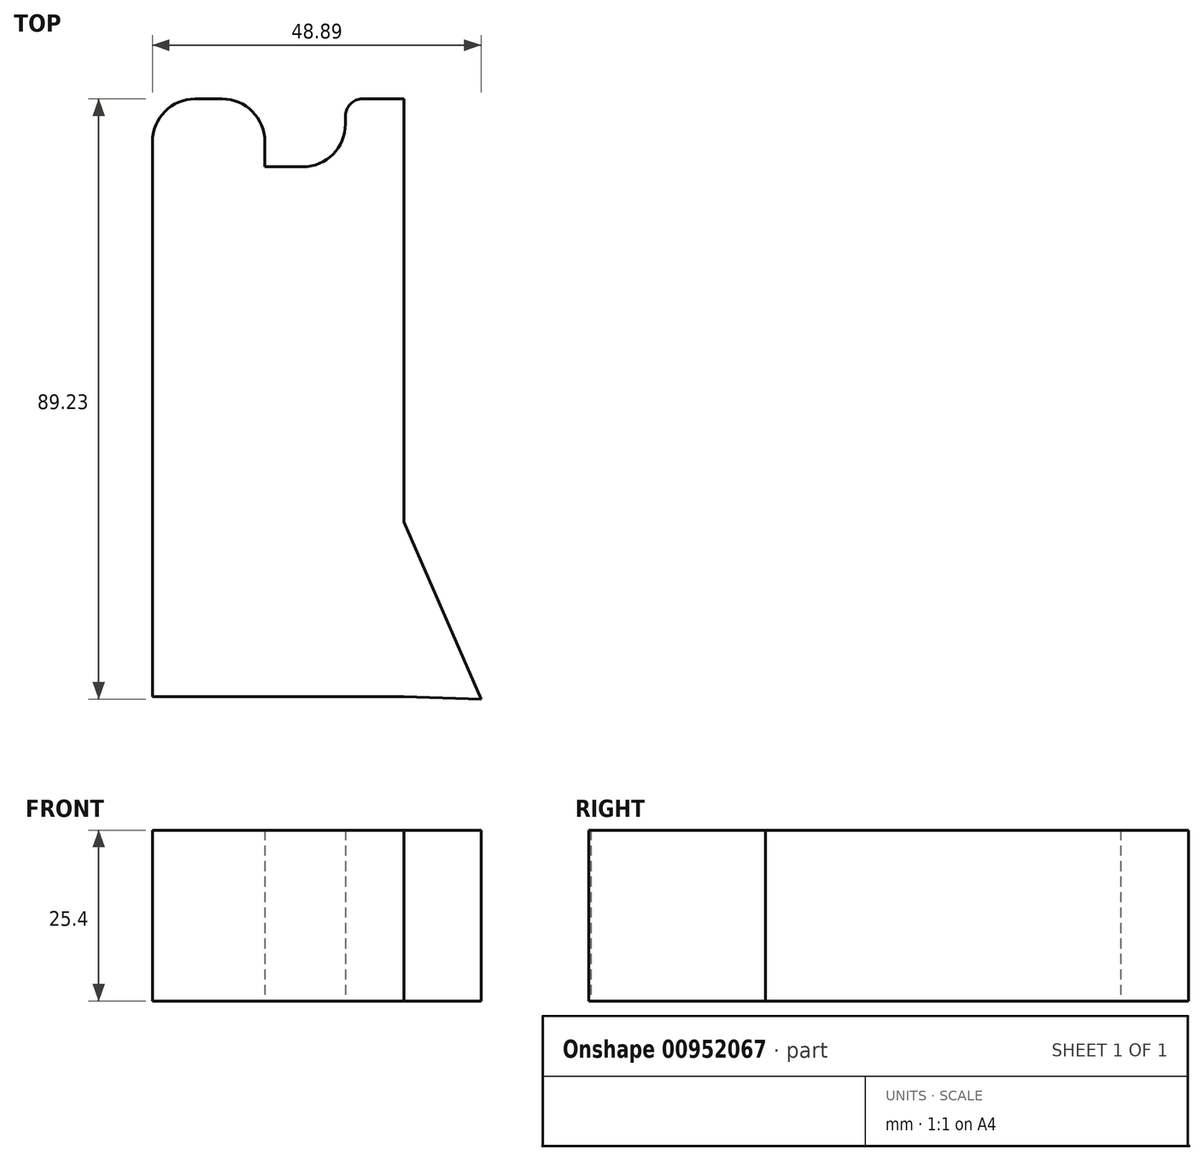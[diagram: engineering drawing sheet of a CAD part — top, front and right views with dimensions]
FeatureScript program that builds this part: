
annotation { "Feature Type Name" : "Feature", "Feature Type Description" : "" }
export const myFeature = defineFeature(function(context is Context, id is Id, definition is map)
    precondition{}
    {
        {
            var Q0;
            Q0=qCreatedBy(makeId("Top.planeOp"),FACE);
            var sketch = newSketch(context, id + "F0", { "sketchPlane" : qUnion([Q0])});
            skLineSegment(sketch, "E0.bottom", {"start": v(-42.54, 32.88) * mm, "end": v(-38.51, 32.88) * mm});
            skLineSegment(sketch, "E0.top", {"start": v(-48.9, -56.01) * mm, "end": v(-11.45, -56.01) * mm});
            skLineSegment(sketch, "E0.left", {"start": v(-48.9, 26.53) * mm, "end": v(-48.9, -56.01) * mm});
            skLineSegment(sketch, "E0.right", {"start": v(-11.45, 32.88) * mm, "end": v(-11.45, -30.05) * mm});
            skLineSegment(sketch, "E1", {"start": v(-11.45, -30.05) * mm, "end": v(0, -56.35) * mm});
            skLineSegment(sketch, "E2", {"start": v(0, -56.35) * mm, "end": v(-11.45, -56.01) * mm});
            skLineSegment(sketch, "E3.top", {"start": v(-32.16, 22.8) * mm, "end": v(-26.52, 22.8) * mm});
            skLineSegment(sketch, "E3.left", {"start": v(-32.16, 26.53) * mm, "end": v(-32.16, 22.8) * mm});
            skLineSegment(sketch, "E3.right", {"start": v(-20.17, 30.34) * mm, "end": v(-20.17, 29.14) * mm});
            skLineSegment(sketch, "E4.trimOffspring", {"start": v(-17.63, 32.88) * mm, "end": v(-11.45, 32.88) * mm});
            skPoint(sketch, "E5.visualSharp", {"position": v(-32.16, 32.88) * mm});
            skArc(sketch, "E5.filletArc", {"start": v(-32.16, 26.53) * mm, "mid": v(-34.02, 31.02) * mm, "end": v(-38.51, 32.88) * mm});
            skPoint(sketch, "E6.visualSharp", {"position": v(-48.9, 32.88) * mm});
            skArc(sketch, "E6.filletArc", {"start": v(-42.54, 32.88) * mm, "mid": v(-47.03, 31.02) * mm, "end": v(-48.9, 26.53) * mm});
            skPoint(sketch, "E7.visualSharp", {"position": v(-20.17, 32.88) * mm});
            skArc(sketch, "E7.filletArc", {"start": v(-17.63, 32.88) * mm, "mid": v(-19.43, 32.14) * mm, "end": v(-20.17, 30.34) * mm});
            skPoint(sketch, "E8.visualSharp", {"position": v(-20.17, 22.8) * mm});
            skArc(sketch, "E8.filletArc", {"start": v(-26.52, 22.8) * mm, "mid": v(-22.03, 24.65) * mm, "end": v(-20.17, 29.14) * mm});
            skSolve(sketch);
        }
        {
            var Q0;
            Q0=makeQuery(id+"F0.imprint","IMPRINT",FACE,{"disambiguationData":[TD([[makeQuery(id+"F0.imprint","IMPRINT",EDGE,{"derivedFrom":sQuery(id+"F0.wireOp",EDGE,"E0.bottom")}),-1.0]])]});
            extrude(context, id + "F1", {"entities" : qUnion([Q0]), "depth" : 25.4 * mm, "offsetDistance" : 25.4 * mm});
        }
    });
